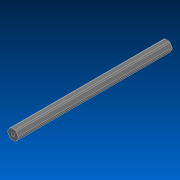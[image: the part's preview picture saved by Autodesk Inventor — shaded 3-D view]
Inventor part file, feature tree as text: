
AUTODESK INVENTOR PART (.ipt)
format: ipt  version: 2022.2 (Build 262287000, 287)  size: 121,856 bytes
history: native  units: in
note: dims shown in document units (in); Inventor stores cm internally (conversion verified against a paired STEP export)
features: extrude x1, sketch x1, other x1
ambient origin geometry x8: Origin, YZ Plane, XZ Plane, XY Plane, X Axis, Y Axis, Z Axis, Center Point
bodies: Solid1 (feature_tree)
feature tree (3):
  extrude  "Extrusion1"  TaperAngle=0.0deg  [1 undecoded]
  sketch  "Sketch1"  dims[d0=28.0in d1=0.0in]
  other  "Cut-Extrude2"
note: 1 required parameter value undecoded (feature->parameter linkage not recoverable at this tier; creation-order binding heuristic only, values carry confidence <= 0.55)
